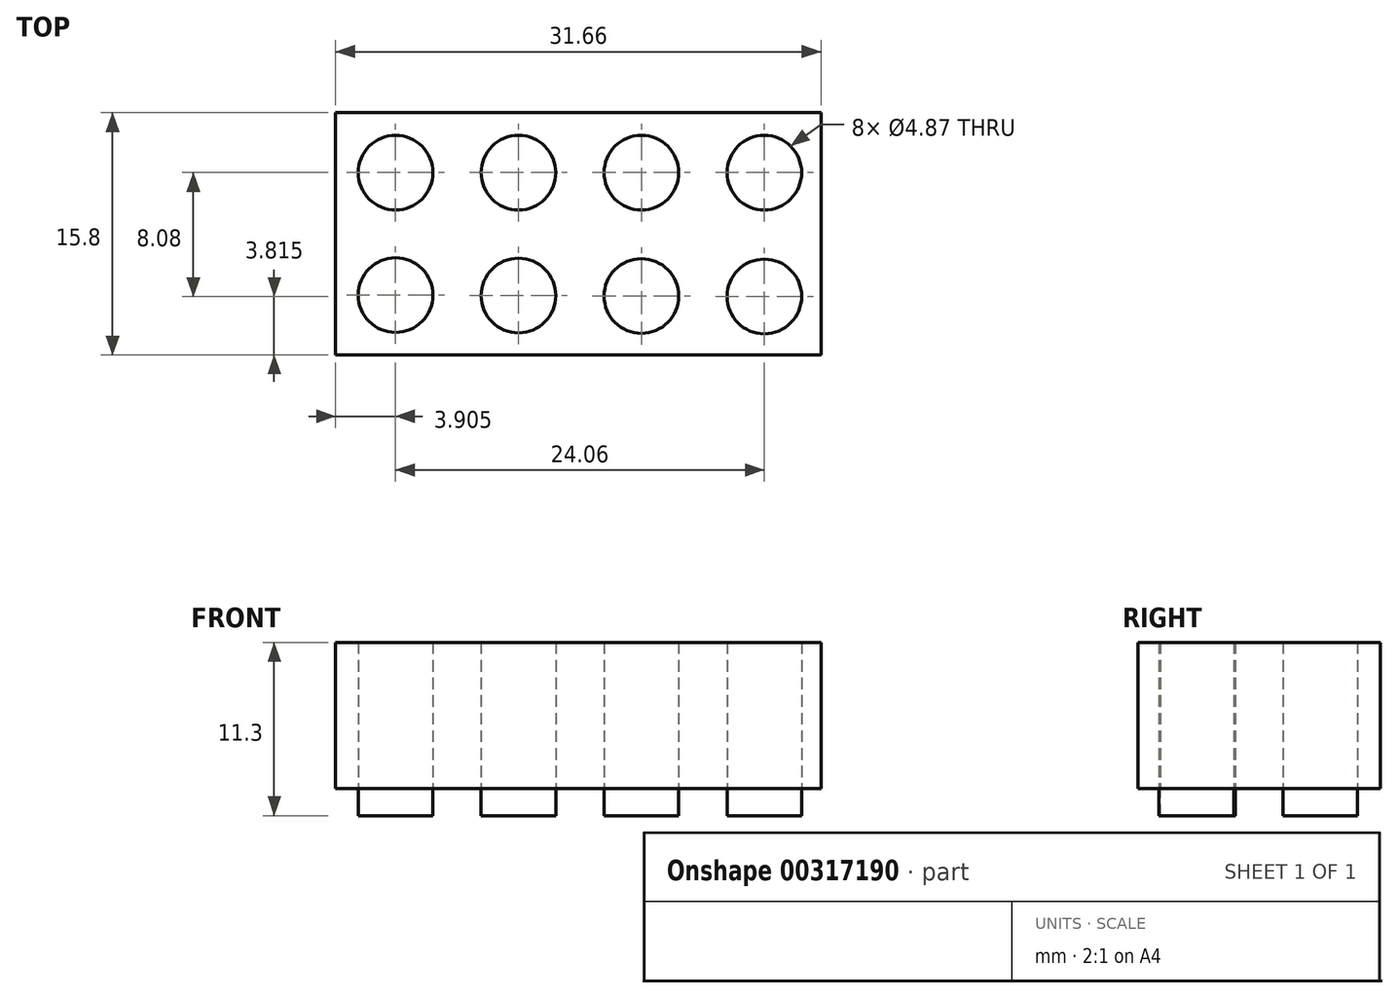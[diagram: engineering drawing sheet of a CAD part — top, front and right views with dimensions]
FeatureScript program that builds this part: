
annotation { "Feature Type Name" : "Feature", "Feature Type Description" : "" }
export const myFeature = defineFeature(function(context is Context, id is Id, definition is map)
    precondition{}
    {
        {
            var Q0;
            Q0=qCreatedBy(makeId("Top.planeOp"),FACE);
            var sketch = newSketch(context, id + "F0", { "sketchPlane" : qUnion([Q0])});
            skLineSegment(sketch, "E0.bottom", {"start": v(-15.83, 7.9) * mm, "end": v(15.83, 7.9) * mm});
            skLineSegment(sketch, "E0.top", {"start": v(-15.83, -7.9) * mm, "end": v(15.83, -7.9) * mm});
            skLineSegment(sketch, "E0.left", {"start": v(-15.83, 7.9) * mm, "end": v(-15.83, -7.9) * mm});
            skLineSegment(sketch, "E0.right", {"start": v(15.83, 7.9) * mm, "end": v(15.83, -7.9) * mm});
            skPoint(sketch, "E0.middle", {"position": v(0, 0) * mm});
            skCircle(sketch, "E1", {"center": v(-11.92, 4) * mm, "radius": 2.44 * mm});
            skCircle(sketch, "E2.1.0.0", {"center": v(-3.9, 4) * mm, "radius": 2.44 * mm});
            skCircle(sketch, "E2.2.0.0", {"center": v(4.11, 4) * mm, "radius": 2.44 * mm});
            skLineSegment(sketch, "E2.direction1", {"start": v(-11.92, 4) * mm, "end": v(-3.9, 4) * mm, "construction": true});
            skCircle(sketch, "E3.0.3.0", {"center": v(12.13, 4) * mm, "radius": 2.44 * mm});
            skCircle(sketch, "E4", {"center": v(-11.93, -4) * mm, "radius": 2.44 * mm});
            skCircle(sketch, "E5.1.0.0", {"center": v(-3.9, -4.02) * mm, "radius": 2.44 * mm});
            skCircle(sketch, "E5.2.0.0", {"center": v(4.11, -4.05) * mm, "radius": 2.44 * mm});
            skLineSegment(sketch, "E5.direction1", {"start": v(-11.93, -4) * mm, "end": v(-3.9, -4.02) * mm, "construction": true});
            skCircle(sketch, "E6.0.3.0", {"center": v(12.13, -4.08) * mm, "radius": 2.44 * mm});
            skSolve(sketch);
        }
        {
            var Q0;
            Q0=makeQuery(id+"F0.imprint","IMPRINT",FACE,{"disambiguationData":[TD([[makeQuery(id+"F0.imprint","IMPRINT",EDGE,{"derivedFrom":sQuery(id+"F0.wireOp",EDGE,"E1")}),1.0]])]});
            var Q1;
            Q1=makeQuery(id+"F0.imprint","IMPRINT",FACE,{"disambiguationData":[TD([[makeQuery(id+"F0.imprint","IMPRINT",EDGE,{"derivedFrom":sQuery(id+"F0.wireOp",EDGE,"E2.1.0.0")}),1.0]])]});
            var Q2;
            Q2=makeQuery(id+"F0.imprint","IMPRINT",FACE,{"disambiguationData":[TD([[makeQuery(id+"F0.imprint","IMPRINT",EDGE,{"derivedFrom":sQuery(id+"F0.wireOp",EDGE,"E4")}),1.0]])]});
            var Q3;
            Q3=makeQuery(id+"F0.imprint","IMPRINT",FACE,{"disambiguationData":[TD([[makeQuery(id+"F0.imprint","IMPRINT",EDGE,{"derivedFrom":sQuery(id+"F0.wireOp",EDGE,"E5.1.0.0")}),1.0]])]});
            var Q4;
            Q4=makeQuery(id+"F0.imprint","IMPRINT",FACE,{"disambiguationData":[TD([[makeQuery(id+"F0.imprint","IMPRINT",EDGE,{"derivedFrom":sQuery(id+"F0.wireOp",EDGE,"E5.2.0.0")}),1.0]])]});
            var Q5;
            Q5=makeQuery(id+"F0.imprint","IMPRINT",FACE,{"disambiguationData":[TD([[makeQuery(id+"F0.imprint","IMPRINT",EDGE,{"derivedFrom":sQuery(id+"F0.wireOp",EDGE,"E2.2.0.0")}),1.0]])]});
            var Q6;
            Q6=makeQuery(id+"F0.imprint","IMPRINT",FACE,{"disambiguationData":[TD([[makeQuery(id+"F0.imprint","IMPRINT",EDGE,{"derivedFrom":sQuery(id+"F0.wireOp",EDGE,"E3.0.3.0")}),1.0]])]});
            var Q7;
            Q7=makeQuery(id+"F0.imprint","IMPRINT",FACE,{"disambiguationData":[TD([[makeQuery(id+"F0.imprint","IMPRINT",EDGE,{"derivedFrom":sQuery(id+"F0.wireOp",EDGE,"E6.0.3.0")}),1.0]])]});
            extrude(context, id + "F1", {"entities" : qUnion([Q0, Q1, Q2, Q3, Q4, Q5, Q6, Q7]), "oppositeDirection" : true, "depth" : 1.77 * mm});
        }
        {
            var Q0;
            Q0 = qSketchRegion(id + "F0", true);
            extrude(context, id + "F2", {"entities" : qUnion([Q0]), "depth" : 9.53 * mm});
        }
    });
